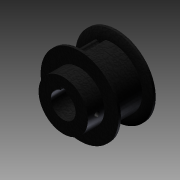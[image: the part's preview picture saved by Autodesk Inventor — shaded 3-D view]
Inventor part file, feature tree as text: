
AUTODESK INVENTOR PART (.ipt)
format: ipt  version: 2012 (Build 160160000, 160)  size: 199,168 bytes
history: native  units: in
note: dims shown in document units (in); Inventor stores cm internally (conversion verified against a paired STEP export)
features: extrude x1, imported_body x1, sketch x1
ambient origin geometry x8: Origin, YZ Plane, XZ Plane, XY Plane, X Axis, Y Axis, Z Axis, Center Point
feature tree (3):
  extrude  "Extrusion1"  Depth=0.0787in
  imported_body  "Base1"
  sketch  "Sketch2"  dims[d1=0.0787in d2=0.0787in d3=0.0394in d4=0.3157in d5=0.2269in d6=0.3937in d7=0.0in d8=0.375in]
